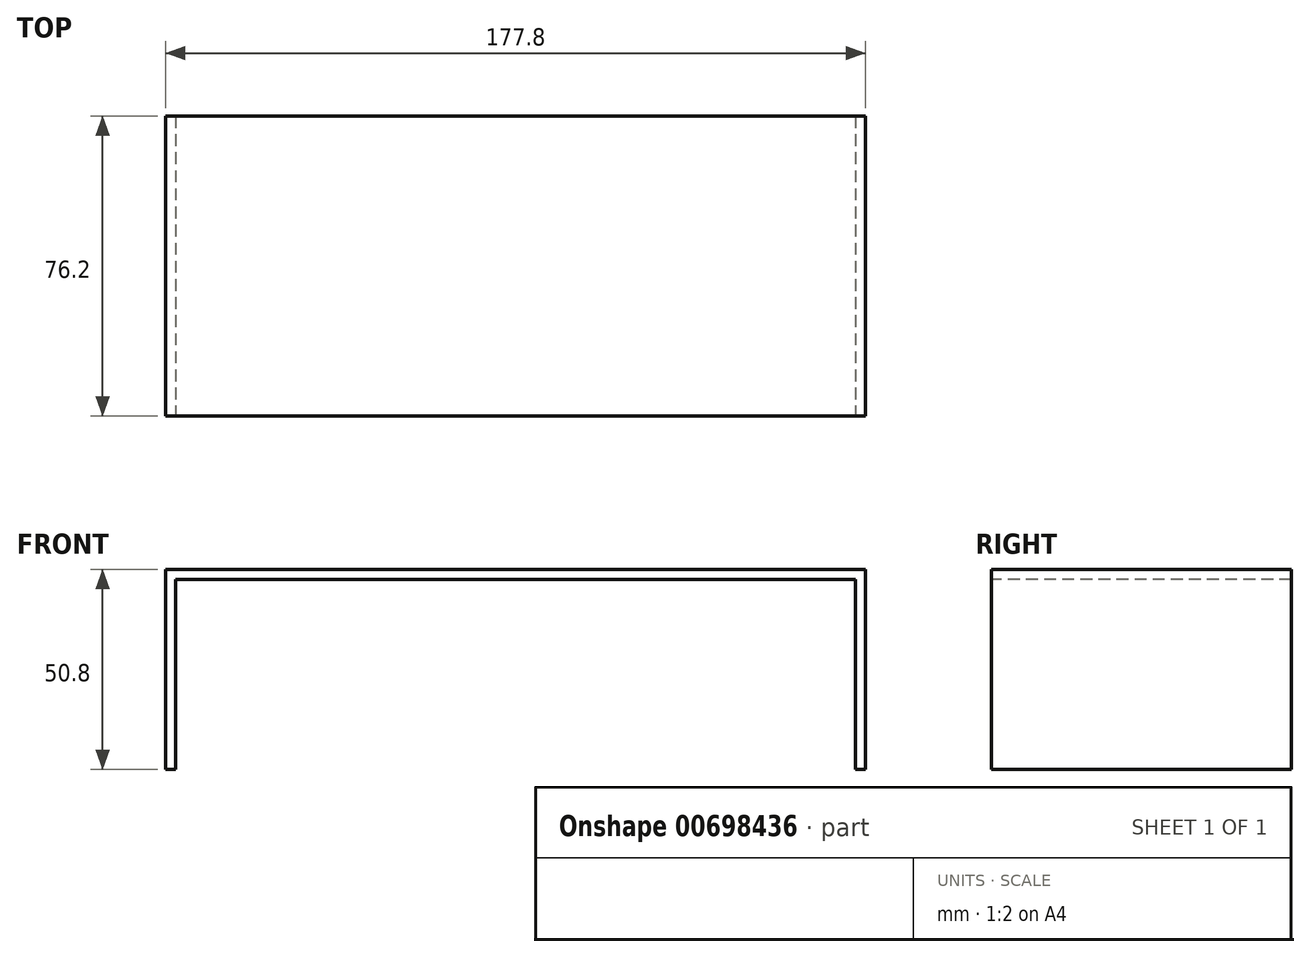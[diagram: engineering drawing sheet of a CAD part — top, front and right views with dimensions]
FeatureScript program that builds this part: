
annotation { "Feature Type Name" : "Feature", "Feature Type Description" : "" }
export const myFeature = defineFeature(function(context is Context, id is Id, definition is map)
    precondition{}
    {
        {
            var Q0;
            Q0=qCreatedBy(makeId("Top.planeOp"),FACE);
            var sketch = newSketch(context, id + "F0", { "sketchPlane" : qUnion([Q0])});
            skLineSegment(sketch, "E0.bottom", {"start": v(-88.9, 38.1) * mm, "end": v(88.9, 38.1) * mm});
            skLineSegment(sketch, "E0.top", {"start": v(-88.9, -38.1) * mm, "end": v(88.9, -38.1) * mm});
            skLineSegment(sketch, "E0.left", {"start": v(-88.9, 38.1) * mm, "end": v(-88.9, -38.1) * mm});
            skLineSegment(sketch, "E0.right", {"start": v(88.9, 38.1) * mm, "end": v(88.9, -38.1) * mm});
            skPoint(sketch, "E0.middle", {"position": v(0, 0) * mm});
            skSolve(sketch);
        }
        {
            var Q0;
            Q0=makeQuery(id+"F0.imprint","IMPRINT",FACE,{"disambiguationData":[TD([[makeQuery(id+"F0.imprint","IMPRINT",EDGE,{"derivedFrom":sQuery(id+"F0.wireOp",EDGE,"E0.bottom")}),-1.0]])]});
            extrude(context, id + "F1", {"entities" : qUnion([Q0]), "depth" : 50.8 * mm, "offsetDistance" : 25.4 * mm});
        }
        {
            var Q0;
            Q0=makeQuery(id+"F1.opExtrude","SWEPT_FACE",FACE,{"disambiguationData":[OSD([sQuery(id+"F0.wireOp",EDGE,"E0.top")])]});
            var Q1;
            Q1=makeQuery(id+"F1.opExtrude","SWEPT_FACE",FACE,{"disambiguationData":[OSD([sQuery(id+"F0.wireOp",EDGE,"E0.bottom")])]});
            var Q2;
            Q2=makeQuery(id+"F1.opExtrude","CAP_FACE",FACE,{"disambiguationData":[OSD([sQuery(id+"F0.wireOp",EDGE,"E0.bottom"),sQuery(id+"F0.wireOp",EDGE,"E0.top"),sQuery(id+"F0.wireOp",EDGE,"E0.left"),sQuery(id+"F0.wireOp",EDGE,"E0.right")])],"isStart":true});
            shell(context, id + "F2", {"entities" : qUnion([Q0, Q1, Q2]), "thickness" : 2.54 * mm});
        }
    });
